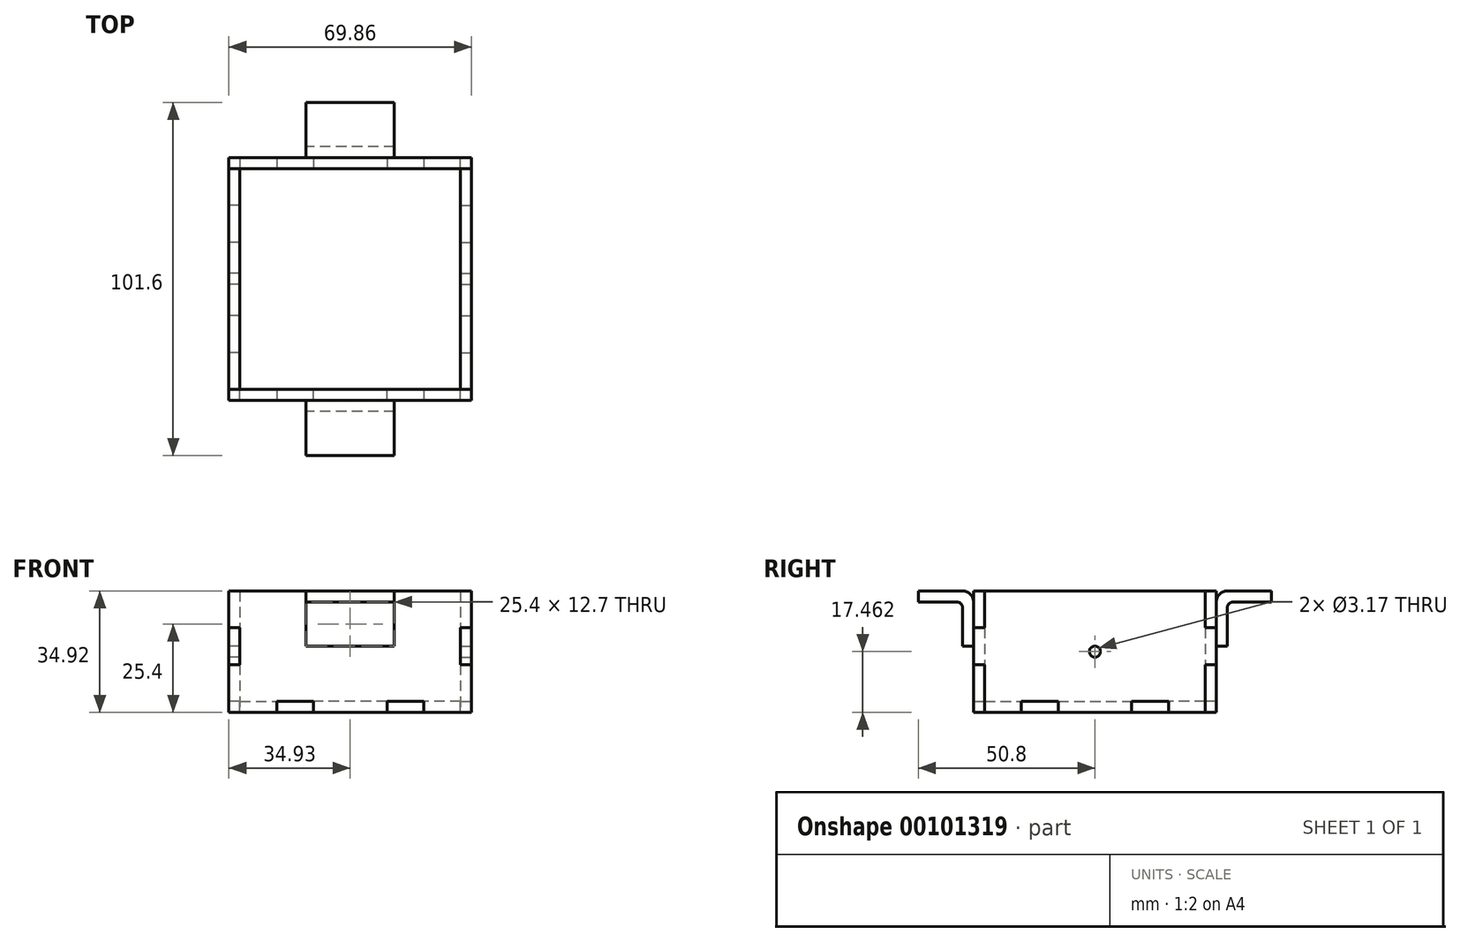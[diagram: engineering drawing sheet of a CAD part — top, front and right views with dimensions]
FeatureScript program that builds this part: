
annotation { "Feature Type Name" : "Feature", "Feature Type Description" : "" }
export const myFeature = defineFeature(function(context is Context, id is Id, definition is map)
    precondition{}
    {
        {
            var Q0;
            Q0=qCreatedBy(makeId("Top.planeOp"),FACE);
            var sketch = newSketch(context, id + "F0", { "sketchPlane" : qUnion([Q0])});
            skLineSegment(sketch, "E0.left", {"start": v(31.75, 31.75) * mm, "end": v(31.75, -31.75) * mm, "construction": true});
            skLineSegment(sketch, "E0.right", {"start": v(-31.75, 31.75) * mm, "end": v(-31.75, -31.75) * mm, "construction": true});
            skPoint(sketch, "E0.middle", {"position": v(0, 0) * mm});
            skLineSegment(sketch, "E1", {"start": v(-31.75, 31.75) * mm, "end": v(-31.75, 21.17) * mm});
            skLineSegment(sketch, "E2", {"start": v(-31.75, 21.17) * mm, "end": v(-34.92, 21.17) * mm});
            skLineSegment(sketch, "E3", {"start": v(-34.92, 21.17) * mm, "end": v(-34.92, 10.58) * mm});
            skLineSegment(sketch, "E4", {"start": v(-34.92, 10.58) * mm, "end": v(-31.75, 10.58) * mm});
            skLineSegment(sketch, "E5", {"start": v(-31.75, 10.58) * mm, "end": v(-31.75, 0) * mm});
            skLineSegment(sketch, "E6", {"start": v(-31.75, 0) * mm, "end": v(31.75, 0) * mm, "construction": true});
            skLineSegment(sketch, "E7", {"start": v(0, 31.75) * mm, "end": v(0, -31.75) * mm, "construction": true});
            skLineSegment(sketch, "E8.MirrorCS", {"start": v(31.75, 31.75) * mm, "end": v(31.75, 21.17) * mm});
            skLineSegment(sketch, "E9.MirrorCS", {"start": v(31.75, 21.17) * mm, "end": v(34.92, 21.17) * mm});
            skLineSegment(sketch, "E10.MirrorCS", {"start": v(34.92, 21.17) * mm, "end": v(34.92, 10.58) * mm});
            skLineSegment(sketch, "E11.MirrorCS", {"start": v(34.92, 10.58) * mm, "end": v(31.75, 10.58) * mm});
            skLineSegment(sketch, "E12.MirrorCS", {"start": v(31.75, 10.58) * mm, "end": v(31.75, 0) * mm});
            skLineSegment(sketch, "E13.MirrorCS", {"start": v(-31.75, -21.17) * mm, "end": v(-34.92, -21.17) * mm});
            skLineSegment(sketch, "E14.MirrorCS", {"start": v(-34.92, -21.17) * mm, "end": v(-34.92, -10.58) * mm});
            skLineSegment(sketch, "E15.MirrorCS", {"start": v(-34.92, -10.58) * mm, "end": v(-31.75, -10.58) * mm});
            skLineSegment(sketch, "E16.MirrorCS", {"start": v(-31.75, -10.58) * mm, "end": v(-31.75, 0) * mm});
            skLineSegment(sketch, "E17.MirrorCS", {"start": v(-31.75, -31.75) * mm, "end": v(-31.75, -21.17) * mm});
            skLineSegment(sketch, "E18.MirrorCS", {"start": v(31.75, -31.75) * mm, "end": v(31.75, -21.17) * mm});
            skLineSegment(sketch, "E19.MirrorCS", {"start": v(31.75, -10.58) * mm, "end": v(31.75, 0) * mm});
            skLineSegment(sketch, "E20.MirrorCS", {"start": v(34.92, -21.17) * mm, "end": v(34.92, -10.58) * mm});
            skLineSegment(sketch, "E21.MirrorCS", {"start": v(34.92, -10.58) * mm, "end": v(31.75, -10.58) * mm});
            skLineSegment(sketch, "E22.MirrorCS", {"start": v(31.75, -21.17) * mm, "end": v(34.92, -21.17) * mm});
            skLineSegment(sketch, "E23", {"start": v(21.17, -31.75) * mm, "end": v(21.17, -34.93) * mm});
            skLineSegment(sketch, "E24", {"start": v(21.17, -34.93) * mm, "end": v(10.58, -34.93) * mm});
            skLineSegment(sketch, "E25", {"start": v(10.58, -34.93) * mm, "end": v(10.58, -31.75) * mm});
            skLineSegment(sketch, "E26", {"start": v(31.75, -31.75) * mm, "end": v(21.17, -31.75) * mm});
            skLineSegment(sketch, "E27", {"start": v(10.58, -31.75) * mm, "end": v(0, -31.75) * mm});
            skLineSegment(sketch, "E28.MirrorCS", {"start": v(-31.75, -31.75) * mm, "end": v(-21.17, -31.75) * mm});
            skLineSegment(sketch, "E29.MirrorCS", {"start": v(-21.17, -31.75) * mm, "end": v(-21.17, -34.93) * mm});
            skLineSegment(sketch, "E30.MirrorCS", {"start": v(-21.17, -34.93) * mm, "end": v(-10.58, -34.93) * mm});
            skLineSegment(sketch, "E31.MirrorCS", {"start": v(-10.58, -34.93) * mm, "end": v(-10.58, -31.75) * mm});
            skLineSegment(sketch, "E32.MirrorCS", {"start": v(-10.58, -31.75) * mm, "end": v(0, -31.75) * mm});
            skLineSegment(sketch, "E33.MirrorCS", {"start": v(31.75, 31.75) * mm, "end": v(21.17, 31.75) * mm});
            skLineSegment(sketch, "E34.MirrorCS", {"start": v(21.17, 31.75) * mm, "end": v(21.17, 34.93) * mm});
            skLineSegment(sketch, "E35.MirrorCS", {"start": v(21.17, 34.93) * mm, "end": v(10.58, 34.93) * mm});
            skLineSegment(sketch, "E36.MirrorCS", {"start": v(10.58, 34.93) * mm, "end": v(10.58, 31.75) * mm});
            skLineSegment(sketch, "E37.MirrorCS", {"start": v(10.58, 31.75) * mm, "end": v(0, 31.75) * mm});
            skLineSegment(sketch, "E38.MirrorCS", {"start": v(-10.58, 31.75) * mm, "end": v(0, 31.75) * mm});
            skLineSegment(sketch, "E39.MirrorCS", {"start": v(-10.58, 34.93) * mm, "end": v(-10.58, 31.75) * mm});
            skLineSegment(sketch, "E40.MirrorCS", {"start": v(-21.17, 34.93) * mm, "end": v(-10.58, 34.93) * mm});
            skLineSegment(sketch, "E41.MirrorCS", {"start": v(-21.17, 31.75) * mm, "end": v(-21.17, 34.93) * mm});
            skLineSegment(sketch, "E42.MirrorCS", {"start": v(-31.75, 31.75) * mm, "end": v(-21.17, 31.75) * mm});
            skSolve(sketch);
        }
        {
            var Q0;
            Q0 = qSketchRegion(id + "F0", true);
            extrude(context, id + "F1", {"entities" : qUnion([Q0]), "depth" : 3.17 * mm});
        }
        {
            var Q0;
            Q0=makeQuery(id+"F1.opExtrude","SWEPT_FACE",FACE,{"disambiguationData":[OSD([sQuery(id+"F0.wireOp",EDGE,"E20.MirrorCS")])]});
            var sketch = newSketch(context, id + "F2", { "sketchPlane" : qUnion([Q0])});
            skLineSegment(sketch, "E43.0", {"start": v(-31.75, 0) * mm, "end": v(-21.17, 0) * mm});
            skLineSegment(sketch, "E43.1", {"start": v(-21.17, 3.18) * mm, "end": v(-21.17, 0) * mm});
            skLineSegment(sketch, "E43.2", {"start": v(-21.17, 3.18) * mm, "end": v(-10.58, 3.18) * mm});
            skLineSegment(sketch, "E43.3", {"start": v(-10.58, 3.18) * mm, "end": v(-10.58, 0) * mm});
            skLineSegment(sketch, "E43.4", {"start": v(-10.58, 0) * mm, "end": v(10.58, 0) * mm});
            skLineSegment(sketch, "E43.5", {"start": v(10.58, 3.18) * mm, "end": v(10.58, 0) * mm});
            skLineSegment(sketch, "E43.6", {"start": v(21.17, 3.18) * mm, "end": v(10.58, 3.18) * mm});
            skLineSegment(sketch, "E43.7", {"start": v(21.17, 3.18) * mm, "end": v(21.17, 0) * mm});
            skLineSegment(sketch, "E43.8", {"start": v(31.75, 0) * mm, "end": v(21.17, 0) * mm});
            skLineSegment(sketch, "E44", {"start": v(-31.75, 0) * mm, "end": v(-31.75, 34.92) * mm, "construction": true});
            skLineSegment(sketch, "E45", {"start": v(-31.75, 34.92) * mm, "end": v(31.75, 34.92) * mm});
            skLineSegment(sketch, "E46", {"start": v(31.75, 34.92) * mm, "end": v(31.75, 0) * mm, "construction": true});
            skLineSegment(sketch, "E47", {"start": v(31.75, 0) * mm, "end": v(31.75, 3.17) * mm});
            skLineSegment(sketch, "E48", {"start": v(31.75, 3.17) * mm, "end": v(31.75, 13.76) * mm});
            skLineSegment(sketch, "E49", {"start": v(31.75, 13.76) * mm, "end": v(34.93, 13.76) * mm});
            skLineSegment(sketch, "E50", {"start": v(34.93, 13.76) * mm, "end": v(34.93, 24.34) * mm});
            skLineSegment(sketch, "E51", {"start": v(34.93, 24.34) * mm, "end": v(31.75, 24.34) * mm});
            skLineSegment(sketch, "E52", {"start": v(31.75, 24.34) * mm, "end": v(31.75, 34.92) * mm});
            skLineSegment(sketch, "E53", {"start": v(0, 0) * mm, "end": v(0, 34.92) * mm, "construction": true});
            skLineSegment(sketch, "E54.MirrorCS", {"start": v(-31.75, 24.34) * mm, "end": v(-31.75, 34.92) * mm});
            skLineSegment(sketch, "E55.MirrorCS", {"start": v(-31.75, 3.17) * mm, "end": v(-31.75, 13.76) * mm});
            skLineSegment(sketch, "E56.MirrorCS", {"start": v(-31.75, 0) * mm, "end": v(-31.75, 3.17) * mm});
            skLineSegment(sketch, "E57.MirrorCS", {"start": v(-31.75, 13.76) * mm, "end": v(-34.93, 13.76) * mm});
            skLineSegment(sketch, "E58.MirrorCS", {"start": v(-34.93, 13.76) * mm, "end": v(-34.93, 24.34) * mm});
            skLineSegment(sketch, "E59.MirrorCS", {"start": v(-34.93, 24.34) * mm, "end": v(-31.75, 24.34) * mm});
            skCircle(sketch, "E60", {"center": v(0, 17.46) * mm, "radius": 1.59 * mm});
            skSolve(sketch);
        }
        {
            var Q0;
            Q0 = qSketchRegion(id + "F2", true);
            var Q1;
            Q1=makeQuery(id+"F1.opExtrude","SWEPT_FACE",FACE,{"disambiguationData":[OSD([sQuery(id+"F0.wireOp",EDGE,"E8.MirrorCS")])]});
            extrude(context, id + "F3", {"entities" : qUnion([Q0]), "endBound" : BoundingType.UP_TO_SURFACE, "oppositeDirection" : true, "endBoundEntityFace" : qUnion([Q1]), "depth" : 25.4 * mm});
        }
        {
            var Q0;
            Q0=makeQuery(id+"F3.opExtrude","SWEPT_BODY",BODY,{"disambiguationData":[OSD([sQuery(id+"F2.wireOp",EDGE,"E43.0"),sQuery(id+"F2.wireOp",EDGE,"E43.1"),sQuery(id+"F2.wireOp",EDGE,"E43.2"),sQuery(id+"F2.wireOp",EDGE,"E43.3"),sQuery(id+"F2.wireOp",EDGE,"E43.4"),sQuery(id+"F2.wireOp",EDGE,"E43.5"),sQuery(id+"F2.wireOp",EDGE,"E43.6"),sQuery(id+"F2.wireOp",EDGE,"E43.7"),sQuery(id+"F2.wireOp",EDGE,"E43.8"),sQuery(id+"F2.wireOp",EDGE,"E45"),sQuery(id+"F2.wireOp",EDGE,"E47"),sQuery(id+"F2.wireOp",EDGE,"E48"),sQuery(id+"F2.wireOp",EDGE,"E49"),sQuery(id+"F2.wireOp",EDGE,"E50"),sQuery(id+"F2.wireOp",EDGE,"E51"),sQuery(id+"F2.wireOp",EDGE,"E52"),sQuery(id+"F2.wireOp",EDGE,"E54.MirrorCS"),sQuery(id+"F2.wireOp",EDGE,"E55.MirrorCS"),sQuery(id+"F2.wireOp",EDGE,"E56.MirrorCS"),sQuery(id+"F2.wireOp",EDGE,"E57.MirrorCS"),sQuery(id+"F2.wireOp",EDGE,"E58.MirrorCS"),sQuery(id+"F2.wireOp",EDGE,"E59.MirrorCS")])]});
            var Q1;
            Q1=qCreatedBy(makeId("Right.planeOp"),FACE);
            mirror(context, id + "F4", {"entities" : qUnion([Q0]), "mirrorPlane" : qUnion([Q1])});
        }
        {
            var Q0;
            Q0=makeQuery(id+"F3.opExtrude","SWEPT_FACE",FACE,{"disambiguationData":[OSD([sQuery(id+"F2.wireOp",EDGE,"E52")])]});
            var sketch = newSketch(context, id + "F5", { "sketchPlane" : qUnion([Q0])});
            skLineSegment(sketch, "E61.0", {"start": v(34.93, 24.34) * mm, "end": v(34.93, 34.92) * mm});
            skLineSegment(sketch, "E61.1", {"start": v(31.75, 24.34) * mm, "end": v(34.92, 24.34) * mm});
            skLineSegment(sketch, "E61.2", {"start": v(31.75, 24.34) * mm, "end": v(31.75, 13.76) * mm});
            skLineSegment(sketch, "E61.3", {"start": v(31.75, 13.76) * mm, "end": v(34.92, 13.76) * mm});
            skLineSegment(sketch, "E61.4", {"start": v(34.93, 0) * mm, "end": v(34.93, 13.76) * mm});
            skLineSegment(sketch, "E61.5", {"start": v(-34.92, 0) * mm, "end": v(-34.92, 13.76) * mm});
            skLineSegment(sketch, "E61.6", {"start": v(-31.75, 13.76) * mm, "end": v(-34.92, 13.76) * mm});
            skLineSegment(sketch, "E61.7", {"start": v(-31.75, 24.34) * mm, "end": v(-31.75, 13.76) * mm});
            skLineSegment(sketch, "E61.8", {"start": v(-31.75, 24.34) * mm, "end": v(-34.92, 24.34) * mm});
            skLineSegment(sketch, "E61.9", {"start": v(-34.92, 24.34) * mm, "end": v(-34.92, 34.92) * mm});
            skLineSegment(sketch, "E61.10", {"start": v(21.17, 3.18) * mm, "end": v(21.17, 0) * mm});
            skLineSegment(sketch, "E61.11", {"start": v(21.17, 3.18) * mm, "end": v(10.58, 3.18) * mm});
            skLineSegment(sketch, "E61.12", {"start": v(10.58, 3.18) * mm, "end": v(10.58, 0) * mm});
            skLineSegment(sketch, "E61.13", {"start": v(10.58, 0) * mm, "end": v(-10.58, 0) * mm});
            skLineSegment(sketch, "E61.14", {"start": v(-10.58, 3.18) * mm, "end": v(-10.58, 0) * mm});
            skLineSegment(sketch, "E61.15", {"start": v(-21.17, 3.18) * mm, "end": v(-10.58, 3.18) * mm});
            skLineSegment(sketch, "E61.16", {"start": v(-21.17, 3.18) * mm, "end": v(-21.17, 0) * mm});
            skLineSegment(sketch, "E62", {"start": v(34.93, 0) * mm, "end": v(21.17, 0) * mm});
            skLineSegment(sketch, "E63", {"start": v(-34.92, 0) * mm, "end": v(-21.17, 0) * mm});
            skLineSegment(sketch, "E64", {"start": v(34.93, 34.92) * mm, "end": v(-34.92, 34.92) * mm});
            skLineSegment(sketch, "E65", {"start": v(-10.58, 0) * mm, "end": v(10.58, 0) * mm});
            skSolve(sketch);
        }
        {
            var Q0;
            Q0 = qSketchRegion(id + "F5", true);
            extrude(context, id + "F6", {"entities" : qUnion([Q0]), "depth" : 3.17 * mm});
        }
        {
            var Q0;
            Q0=makeQuery(id+"F6.opExtrude","SWEPT_BODY",BODY,{"disambiguationData":[OSD([sQuery(id+"F5.wireOp",EDGE,"E61.0"),sQuery(id+"F5.wireOp",EDGE,"E61.1"),sQuery(id+"F5.wireOp",EDGE,"E61.2"),sQuery(id+"F5.wireOp",EDGE,"E61.3"),sQuery(id+"F5.wireOp",EDGE,"E61.4"),sQuery(id+"F5.wireOp",EDGE,"E61.5"),sQuery(id+"F5.wireOp",EDGE,"E61.6"),sQuery(id+"F5.wireOp",EDGE,"E61.7"),sQuery(id+"F5.wireOp",EDGE,"E61.8"),sQuery(id+"F5.wireOp",EDGE,"E61.9"),sQuery(id+"F5.wireOp",EDGE,"E61.10"),sQuery(id+"F5.wireOp",EDGE,"E61.11"),sQuery(id+"F5.wireOp",EDGE,"E61.12"),sQuery(id+"F5.wireOp",EDGE,"E61.14"),sQuery(id+"F5.wireOp",EDGE,"E61.15"),sQuery(id+"F5.wireOp",EDGE,"E61.16"),sQuery(id+"F5.wireOp",EDGE,"E62"),sQuery(id+"F5.wireOp",EDGE,"E63"),sQuery(id+"F5.wireOp",EDGE,"E64"),sQuery(id+"F5.wireOp",EDGE,"E65")])]});
            var Q1;
            Q1=qCreatedBy(makeId("Front.planeOp"),FACE);
            mirror(context, id + "F7", {"entities" : qUnion([Q0]), "mirrorPlane" : qUnion([Q1])});
        }
        {
            var Q0;
            Q0=qCreatedBy(makeId("Right.planeOp"),FACE);
            var sketch = newSketch(context, id + "F8", { "sketchPlane" : qUnion([Q0])});
            skLineSegment(sketch, "E66", {"start": v(-34.92, 31.75) * mm, "end": v(-34.92, 19.05) * mm});
            skLineSegment(sketch, "E67", {"start": v(-34.92, 19.05) * mm, "end": v(-38.1, 19.05) * mm});
            skLineSegment(sketch, "E68", {"start": v(-38.1, 19.05) * mm, "end": v(-38.1, 30.16) * mm});
            skLineSegment(sketch, "E69", {"start": v(-39.69, 31.75) * mm, "end": v(-50.8, 31.75) * mm});
            skLineSegment(sketch, "E70", {"start": v(-50.8, 31.75) * mm, "end": v(-50.8, 34.92) * mm});
            skLineSegment(sketch, "E71", {"start": v(-50.8, 34.92) * mm, "end": v(-38.1, 34.92) * mm});
            skPoint(sketch, "E72.visualSharp", {"position": v(-34.92, 34.92) * mm});
            skArc(sketch, "E72.filletArc", {"start": v(-34.92, 31.75) * mm, "mid": v(-35.85, 34) * mm, "end": v(-38.1, 34.92) * mm});
            skArc(sketch, "E73.filletArc", {"start": v(-38.1, 30.16) * mm, "mid": v(-38.56, 31.29) * mm, "end": v(-39.69, 31.75) * mm});
            skSolve(sketch);
        }
        {
            var Q0;
            Q0 = qSketchRegion(id + "F8", true);
            extrude(context, id + "F9", {"entities" : qUnion([Q0]), "depth" : 12.7 * mm, "hasSecondDirection" : true, "secondDirectionOppositeDirection" : true, "secondDirectionDepth" : 12.7 * mm});
        }
        {
            var Q0;
            Q0=makeQuery(id+"F9.opExtrude","SWEPT_BODY",BODY,{"disambiguationData":[OSD([sQuery(id+"F8.wireOp",EDGE,"E66"),sQuery(id+"F8.wireOp",EDGE,"E67"),sQuery(id+"F8.wireOp",EDGE,"E68"),sQuery(id+"F8.wireOp",EDGE,"E69"),sQuery(id+"F8.wireOp",EDGE,"E70"),sQuery(id+"F8.wireOp",EDGE,"E71"),sQuery(id+"F8.wireOp",EDGE,"E72.filletArc"),sQuery(id+"F8.wireOp",EDGE,"E73.filletArc")])]});
            var Q1;
            Q1=qCreatedBy(makeId("Front.planeOp"),FACE);
            mirror(context, id + "F10", {"operationType" : NewBodyOperationType.ADD, "entities" : qUnion([Q0]), "mirrorPlane" : qUnion([Q1])});
        }
    });
